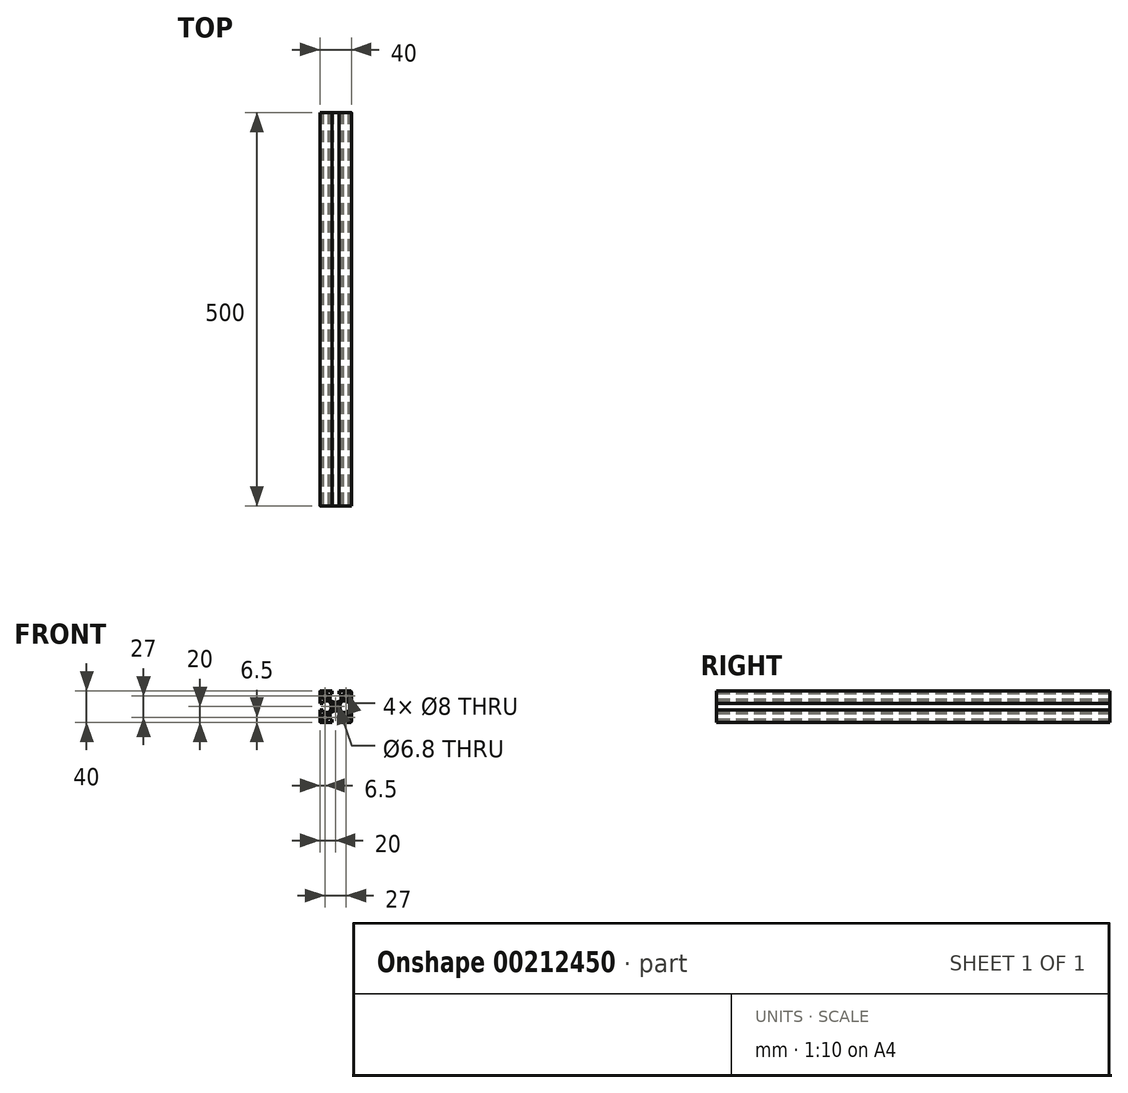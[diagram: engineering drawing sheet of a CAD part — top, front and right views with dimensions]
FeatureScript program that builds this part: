
annotation { "Feature Type Name" : "Feature", "Feature Type Description" : "" }
export const myFeature = defineFeature(function(context is Context, id is Id, definition is map)
    precondition{}
    {
        {
            assignVariable(context, id + "F0", {"name" : "L", "anyValue" : 500});
        }
        {
            var Q0;
            Q0=qCreatedBy(makeId("Front.planeOp"),FACE);
            var sketch = newSketch(context, id + "F1", { "sketchPlane" : qUnion([Q0])});
            skLineSegment(sketch, "E0.bottom", {"start": v(20, 20) * mm, "end": v(-20, 20) * mm});
            skLineSegment(sketch, "E0.top", {"start": v(20, -20) * mm, "end": v(-20, -20) * mm});
            skLineSegment(sketch, "E0.left", {"start": v(20, 20) * mm, "end": v(20, -20) * mm});
            skLineSegment(sketch, "E0.right", {"start": v(-20, 20) * mm, "end": v(-20, -20) * mm});
            skPoint(sketch, "E0.middle", {"position": v(0, 0) * mm});
            skSolve(sketch);
        }
        {
            var Q0;
            Q0=qSketchRegion(id+"F1",true);
            extrude(context, id + "F2", {"entities" : qUnion([Q0]), "endBound" : BoundingType.SYMMETRIC, "depth" : (getVariable(context, 'L')) * mm});
        }
        {
            var Q0;
            Q0=qCreatedBy(makeId("Front.planeOp"),FACE);
            var sketch = newSketch(context, id + "F3", { "sketchPlane" : qUnion([Q0])});
            skLineSegment(sketch, "E1.bottom", {"start": v(13.5, 13.5) * mm, "end": v(-13.5, 13.5) * mm, "construction": true});
            skLineSegment(sketch, "E1.top", {"start": v(13.5, -13.5) * mm, "end": v(-13.5, -13.5) * mm, "construction": true});
            skLineSegment(sketch, "E1.left", {"start": v(13.5, 13.5) * mm, "end": v(13.5, -13.5) * mm, "construction": true});
            skLineSegment(sketch, "E1.right", {"start": v(-13.5, 13.5) * mm, "end": v(-13.5, -13.5) * mm, "construction": true});
            skPoint(sketch, "E1.middle", {"position": v(0, 0) * mm});
            skCircle(sketch, "E2", {"center": v(-13.5, 13.5) * mm, "radius": 4 * mm});
            skCircle(sketch, "E3", {"center": v(-13.5, -13.5) * mm, "radius": 4 * mm});
            skCircle(sketch, "E4", {"center": v(13.5, -13.5) * mm, "radius": 4 * mm});
            skCircle(sketch, "E5", {"center": v(13.5, 13.5) * mm, "radius": 4 * mm});
            skCircle(sketch, "E6", {"center": v(0, 0) * mm, "radius": 3.4 * mm});
            skSolve(sketch);
        }
        {
            var Q0;
            Q0=qSketchRegion(id+"F3",true);
            extrude(context, id + "F4", {"entities" : qUnion([Q0]), "operationType" : NewBodyOperationType.REMOVE, "endBound" : BoundingType.THROUGH_ALL, "oppositeDirection" : true, "depth" : 25 * mm, "hasSecondDirection" : true, "secondDirectionBound" : SecondDirectionBoundingType.THROUGH_ALL, "secondDirectionOppositeDirection" : false, "secondDirectionDepth" : 25 * mm});
        }
        {
            var Q0;
            Q0=qCreatedBy(makeId("Front.planeOp"),FACE);
            var sketch = newSketch(context, id + "F5", { "sketchPlane" : qUnion([Q0])});
            skLineSegment(sketch, "E7", {"start": v(-4.2, 20) * mm, "end": v(4.2, 20) * mm});
            skLineSegment(sketch, "E8", {"start": v(4.2, 20) * mm, "end": v(4.2, 16) * mm});
            skLineSegment(sketch, "E9", {"start": v(4.2, 16) * mm, "end": v(7.25, 16) * mm});
            skLineSegment(sketch, "E10", {"start": v(7.25, 16) * mm, "end": v(7.25, 8.86) * mm});
            skLineSegment(sketch, "E11", {"start": v(-4.2, 20) * mm, "end": v(-4.2, 16) * mm});
            skLineSegment(sketch, "E12", {"start": v(-4.2, 16) * mm, "end": v(-7.25, 16) * mm});
            skLineSegment(sketch, "E13", {"start": v(-7.25, 16) * mm, "end": v(-7.25, 8.86) * mm});
            skLineSegment(sketch, "E14", {"start": v(0, 20) * mm, "end": v(0, -0.42) * mm, "construction": true});
            skLineSegment(sketch, "E15", {"start": v(-3.21, 5.5) * mm, "end": v(3.16, 5.5) * mm, "construction": true});
            skArc(sketch, "E16", {"start": v(-7.25, 8.86) * mm, "mid": v(0, 5.5) * mm, "end": v(7.25, 8.86) * mm});
            skLineSegment(sketch, "E17.1.0", {"start": v(-16, 4.2) * mm, "end": v(-16, 7.25) * mm});
            skLineSegment(sketch, "E17.1.1", {"start": v(-16, -7.25) * mm, "end": v(-8.86, -7.25) * mm});
            skLineSegment(sketch, "E17.1.2", {"start": v(-20, -4.2) * mm, "end": v(-20, 4.2) * mm});
            skLineSegment(sketch, "E17.1.3", {"start": v(-16, 7.25) * mm, "end": v(-8.86, 7.25) * mm});
            skLineSegment(sketch, "E17.1.4", {"start": v(-20, 4.2) * mm, "end": v(-16, 4.2) * mm});
            skLineSegment(sketch, "E17.1.5", {"start": v(-20, -4.2) * mm, "end": v(-16, -4.2) * mm});
            skLineSegment(sketch, "E17.1.6", {"start": v(-16, -4.2) * mm, "end": v(-16, -7.25) * mm});
            skArc(sketch, "E17.1.7", {"start": v(-8.86, -7.25) * mm, "mid": v(-5.5, 0) * mm, "end": v(-8.86, 7.25) * mm});
            skLineSegment(sketch, "E17.1.8", {"start": v(-5.5, -3.21) * mm, "end": v(-5.5, 3.16) * mm, "construction": true});
            skLineSegment(sketch, "E17.2.0", {"start": v(-4.2, -16) * mm, "end": v(-7.25, -16) * mm});
            skLineSegment(sketch, "E17.2.1", {"start": v(7.25, -16) * mm, "end": v(7.25, -8.86) * mm});
            skLineSegment(sketch, "E17.2.2", {"start": v(4.2, -20) * mm, "end": v(-4.2, -20) * mm});
            skLineSegment(sketch, "E17.2.3", {"start": v(-7.25, -16) * mm, "end": v(-7.25, -8.86) * mm});
            skLineSegment(sketch, "E17.2.4", {"start": v(-4.2, -20) * mm, "end": v(-4.2, -16) * mm});
            skLineSegment(sketch, "E17.2.5", {"start": v(4.2, -20) * mm, "end": v(4.2, -16) * mm});
            skLineSegment(sketch, "E17.2.6", {"start": v(4.2, -16) * mm, "end": v(7.25, -16) * mm});
            skArc(sketch, "E17.2.7", {"start": v(7.25, -8.86) * mm, "mid": v(0, -5.5) * mm, "end": v(-7.25, -8.86) * mm});
            skLineSegment(sketch, "E17.2.8", {"start": v(3.21, -5.5) * mm, "end": v(-3.16, -5.5) * mm, "construction": true});
            skLineSegment(sketch, "E17.3.0", {"start": v(16, -4.2) * mm, "end": v(16, -7.25) * mm});
            skLineSegment(sketch, "E17.3.1", {"start": v(16, 7.25) * mm, "end": v(8.86, 7.25) * mm});
            skLineSegment(sketch, "E17.3.2", {"start": v(20, 4.2) * mm, "end": v(20, -4.2) * mm});
            skLineSegment(sketch, "E17.3.3", {"start": v(16, -7.25) * mm, "end": v(8.86, -7.25) * mm});
            skLineSegment(sketch, "E17.3.4", {"start": v(20, -4.2) * mm, "end": v(16, -4.2) * mm});
            skLineSegment(sketch, "E17.3.5", {"start": v(20, 4.2) * mm, "end": v(16, 4.2) * mm});
            skLineSegment(sketch, "E17.3.6", {"start": v(16, 4.2) * mm, "end": v(16, 7.25) * mm});
            skArc(sketch, "E17.3.7", {"start": v(8.86, 7.25) * mm, "mid": v(5.5, 0) * mm, "end": v(8.86, -7.25) * mm});
            skLineSegment(sketch, "E17.3.8", {"start": v(5.5, 3.21) * mm, "end": v(5.5, -3.16) * mm, "construction": true});
            skPoint(sketch, "E17.center", {"position": v(0, 0) * mm});
            skSolve(sketch);
        }
        {
            var Q0;
            Q0=qSketchRegion(id+"F5",true);
            extrude(context, id + "F6", {"entities" : qUnion([Q0]), "operationType" : NewBodyOperationType.REMOVE, "endBound" : BoundingType.THROUGH_ALL, "oppositeDirection" : true, "depth" : 25 * mm, "hasSecondDirection" : true, "secondDirectionBound" : SecondDirectionBoundingType.THROUGH_ALL, "secondDirectionOppositeDirection" : false, "secondDirectionDepth" : 25 * mm});
        }
        {
            var Q0;
            Q0=makeQuery(id+"F2.opExtrude","SWEPT_EDGE",EDGE,{"disambiguationData":[OSD([sQuery(id+"F1.wireOp",EDGE,"E0.bottom"),sQuery(id+"F1.wireOp",EDGE,"E0.right")])]});
            var Q1;
            Q1=makeQuery(id+"F2.opExtrude","SWEPT_EDGE",EDGE,{"disambiguationData":[OSD([sQuery(id+"F1.wireOp",EDGE,"E0.bottom"),sQuery(id+"F1.wireOp",EDGE,"E0.left")])]});
            var Q2;
            Q2=makeQuery(id+"F2.opExtrude","SWEPT_EDGE",EDGE,{"disambiguationData":[OSD([sQuery(id+"F1.wireOp",EDGE,"E0.top"),sQuery(id+"F1.wireOp",EDGE,"E0.left")])]});
            var Q3;
            Q3=makeQuery(id+"F2.opExtrude","SWEPT_EDGE",EDGE,{"disambiguationData":[OSD([sQuery(id+"F1.wireOp",EDGE,"E0.top"),sQuery(id+"F1.wireOp",EDGE,"E0.right")])]});
            fillet(context, id + "F7", {"entities" : qUnion([Q0, Q1, Q2, Q3]), "radius" : 1 * mm, "tangentPropagation" : true, "allowEdgeOverflow" : false});
        }
    });
